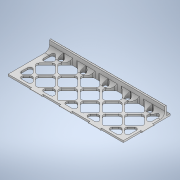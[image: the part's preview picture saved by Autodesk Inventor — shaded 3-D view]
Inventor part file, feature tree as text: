
AUTODESK INVENTOR PART (.ipt)
format: ipt  version: 2020 (Build 240168000, 168)  size: 716,288 bytes
history: native  units: in
note: dims shown in document units (in); Inventor stores cm internally (conversion verified against a paired STEP export)
features: extrude x6, sketch x6, fillet x5
ambient origin geometry x8: Origin, YZ Plane, XZ Plane, XY Plane, X Axis, Y Axis, Z Axis, Center Point
bodies: Solid1 (feature_tree)
feature tree (17):
  extrude  "Extrusion1"  Depth=1.5748in
  extrude  "Extrusion2"  Depth=0.9843in
  extrude  "Extrusion3"  Depth=0.9843in
  fillet  "Fillet3"  Radius=0.1969in
  extrude  "Extrusion4"  Depth=0.0591in
  fillet  "Fillet4"  Radius=0.1969in
  fillet  "Fillet5"  Radius=0.3937in
  fillet  "Fillet6"  Radius=0.0591in
  extrude  "Extrusion5"  Depth=0.3937in
  extrude  "Extrusion6"  Depth=0.0591in
  fillet  "Fillet7"  Radius=0.0591in
  sketch  "Sketch1"  dims[d0=3.937in d1=1.5748in]
  sketch  "Sketch2"  dims[d2=0.9843in d3=0.9843in]
  sketch  "Sketch3"  dims[d4=0.9843in d5=0.9843in d6=0.1969in]
  sketch  "Sketch4"  dims[d7=0.3937in d8=0.0591in d9=0.1969in d10=0.3937in d11=0.0591in]
  sketch  "Sketch5"  dims[d12=0.1969in d13=0.3937in]
  sketch  "Sketch6"  dims[d14=0.0591in d15=0.1969in d16=0.0591in d17=0.3937in d18=0.1969in d19=0.0591in d20=0.3937in d27=0.0984in d28=0.748in d29=0.748in d30=0.748in d31=0.748in d32=0.748in d33=0.0984in d34=0.0394in d35=1.9685in d37=0.748in d38=0.3937in d40=1.0in d42=135.0deg d43=1.5748in d45=0.748in d46=0.3937in d48=1.0in d50=1.9685in d52=0.748in d53=0.3937in d55=1.0in d57=0.3937in d58=0.0591in d59=0.3937in d60=0.0591in d61=0.3937in d62=0.0591in d63=0.0591in d64=0.0in d67=0.1969in d68=0.0591in d69=0.3937in d70=0.0591in d71=0.0in d72=0.1181in d73=0.0591in d74=0.0591in d75=0.0in d76=0.0787in d77=0.0591in d78=0.315in d79=0.0in d80=0.0276in d81=0.1575in d82=0.0591in d83=0.0591in d84=0.315in d85=0.157in d86=0.0in d87=0.0in d88=0.1969in d89=0.0591in d90=0.0591in d91=0.0in d92=0.0591in d44=0.5in]
